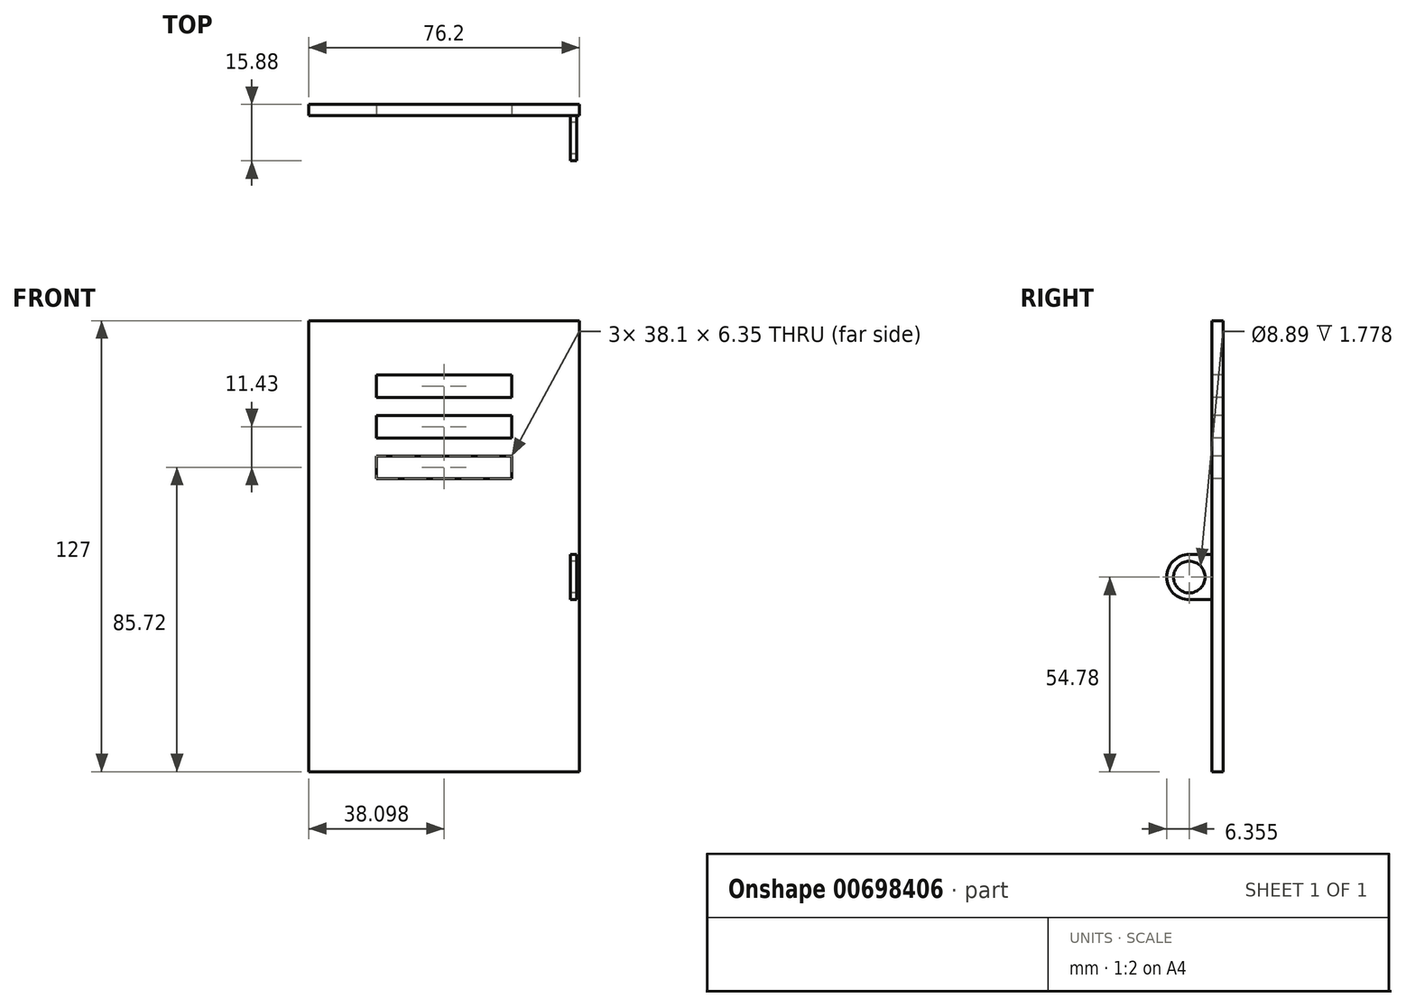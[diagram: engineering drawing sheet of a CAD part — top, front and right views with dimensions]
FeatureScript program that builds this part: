
annotation { "Feature Type Name" : "Feature", "Feature Type Description" : "" }
export const myFeature = defineFeature(function(context is Context, id is Id, definition is map)
    precondition{}
    {
        {
            var Q0;
            Q0=qCreatedBy(makeId("Front.planeOp"),FACE);
            var sketch = newSketch(context, id + "F0", { "sketchPlane" : qUnion([Q0])});
            skLineSegment(sketch, "E0.bottom", {"start": v(-36.9, 78.57) * mm, "end": v(39.3, 78.57) * mm});
            skLineSegment(sketch, "E0.top", {"start": v(-36.9, -48.43) * mm, "end": v(39.3, -48.43) * mm});
            skLineSegment(sketch, "E0.left", {"start": v(-36.9, 78.57) * mm, "end": v(-36.9, -48.43) * mm});
            skLineSegment(sketch, "E0.right", {"start": v(39.3, 78.57) * mm, "end": v(39.3, -48.43) * mm});
            skSolve(sketch);
        }
        {
            var Q0;
            Q0=makeQuery(id+"F0.imprint","IMPRINT",FACE,{"disambiguationData":[TD([[makeQuery(id+"F0.imprint","IMPRINT",EDGE,{"derivedFrom":sQuery(id+"F0.wireOp",EDGE,"E0.bottom")}),-1.0]])]});
            extrude(context, id + "F1", {"entities" : qUnion([Q0]), "depth" : 3.17 * mm, "offsetDistance" : 25.4 * mm});
        }
        {
            var Q0;
            Q0=makeQuery(id+"F1.opExtrude","CAP_FACE",FACE,{"disambiguationData":[OSD([sQuery(id+"F0.wireOp",EDGE,"E0.bottom"),sQuery(id+"F0.wireOp",EDGE,"E0.top"),sQuery(id+"F0.wireOp",EDGE,"E0.left"),sQuery(id+"F0.wireOp",EDGE,"E0.right")])],"isStart":false});
            var sketch = newSketch(context, id + "F2", { "sketchPlane" : qUnion([Q0])});
            skLineSegment(sketch, "E1.bottom", {"start": v(-17.84, 63.33) * mm, "end": v(20.26, 63.33) * mm});
            skLineSegment(sketch, "E1.top", {"start": v(-17.84, 56.98) * mm, "end": v(20.26, 56.98) * mm});
            skLineSegment(sketch, "E1.left", {"start": v(-17.84, 63.33) * mm, "end": v(-17.84, 56.98) * mm});
            skLineSegment(sketch, "E1.right", {"start": v(20.26, 63.33) * mm, "end": v(20.26, 56.98) * mm});
            skLineSegment(sketch, "E2.bottom", {"start": v(-17.84, 51.9) * mm, "end": v(20.26, 51.9) * mm});
            skLineSegment(sketch, "E2.top", {"start": v(-17.84, 45.55) * mm, "end": v(20.26, 45.55) * mm});
            skLineSegment(sketch, "E2.left", {"start": v(-17.84, 51.9) * mm, "end": v(-17.84, 45.55) * mm});
            skLineSegment(sketch, "E2.right", {"start": v(20.26, 51.9) * mm, "end": v(20.26, 45.55) * mm});
            skLineSegment(sketch, "E3.bottom", {"start": v(-17.84, 40.47) * mm, "end": v(20.26, 40.47) * mm});
            skLineSegment(sketch, "E3.top", {"start": v(-17.84, 34.12) * mm, "end": v(20.26, 34.12) * mm});
            skLineSegment(sketch, "E3.left", {"start": v(-17.84, 40.47) * mm, "end": v(-17.84, 34.12) * mm});
            skLineSegment(sketch, "E3.right", {"start": v(20.26, 40.47) * mm, "end": v(20.26, 34.12) * mm});
            skSolve(sketch);
        }
        {
            var Q0;
            Q0=makeQuery(id+"F2.imprint","IMPRINT",FACE,{"disambiguationData":[TD([[makeQuery(id+"F2.imprint","IMPRINT",EDGE,{"derivedFrom":sQuery(id+"F2.wireOp",EDGE,"E1.bottom")}),-1.0]])]});
            var Q1;
            Q1=makeQuery(id+"F2.imprint","IMPRINT",FACE,{"disambiguationData":[TD([[makeQuery(id+"F2.imprint","IMPRINT",EDGE,{"derivedFrom":sQuery(id+"F2.wireOp",EDGE,"E2.bottom")}),-1.0]])]});
            var Q2;
            Q2=makeQuery(id+"F2.imprint","IMPRINT",FACE,{"disambiguationData":[TD([[makeQuery(id+"F2.imprint","IMPRINT",EDGE,{"derivedFrom":sQuery(id+"F2.wireOp",EDGE,"E3.bottom")}),-1.0]])]});
            extrude(context, id + "F3", {"entities" : qUnion([Q0, Q1, Q2]), "operationType" : NewBodyOperationType.REMOVE, "oppositeDirection" : true, "depth" : 3.17 * mm, "offsetDistance" : 25.4 * mm});
        }
        {
            var Q0;
            Q0=makeQuery(id+"F1.opExtrude","CAP_FACE",FACE,{"disambiguationData":[OSD([sQuery(id+"F0.wireOp",EDGE,"E0.bottom"),sQuery(id+"F0.wireOp",EDGE,"E0.top"),sQuery(id+"F0.wireOp",EDGE,"E0.left"),sQuery(id+"F0.wireOp",EDGE,"E0.right")])],"isStart":false});
            var sketch = newSketch(context, id + "F4", { "sketchPlane" : qUnion([Q0])});
            skLineSegment(sketch, "E4.bottom", {"start": v(38.55, 12.7) * mm, "end": v(36.77, 12.7) * mm});
            skLineSegment(sketch, "E4.top", {"start": v(38.55, 0) * mm, "end": v(36.77, 0) * mm});
            skLineSegment(sketch, "E4.left", {"start": v(38.55, 12.7) * mm, "end": v(38.55, 0) * mm});
            skLineSegment(sketch, "E4.right", {"start": v(36.77, 12.7) * mm, "end": v(36.77, 0) * mm});
            skSolve(sketch);
        }
        {
            var Q0;
            Q0=makeQuery(id+"F4.imprint","IMPRINT",FACE,{"disambiguationData":[TD([[makeQuery(id+"F4.imprint","IMPRINT",EDGE,{"derivedFrom":sQuery(id+"F4.wireOp",EDGE,"E4.bottom")}),1.0]])]});
            extrude(context, id + "F5", {"entities" : qUnion([Q0]), "operationType" : NewBodyOperationType.ADD, "depth" : 12.7 * mm, "offsetDistance" : 25.4 * mm});
        }
        {
            var Q0;
            Q0=makeQuery(id+"F5.opExtrude","CAP_EDGE",EDGE,{"disambiguationData":[OSD([sQuery(id+"F4.wireOp",EDGE,"E4.bottom")])],"isStart":false});
            fillet(context, id + "F6", {"entities" : qUnion([Q0]), "radius" : 6.35 * mm, "tangentPropagation" : true, "allowEdgeOverflow" : false});
        }
        {
            var Q0;
            Q0=makeQuery(id+"F5.opExtrude","CAP_EDGE",EDGE,{"disambiguationData":[OSD([sQuery(id+"F4.wireOp",EDGE,"E4.top")])],"isStart":false});
            fillet(context, id + "F7", {"entities" : qUnion([Q0]), "radius" : 6.35 * mm, "tangentPropagation" : true, "allowEdgeOverflow" : false});
        }
        {
            var Q0;
            Q0=makeQuery(id+"F5.opExtrude","SWEPT_FACE",FACE,{"disambiguationData":[OSD([sQuery(id+"F4.wireOp",EDGE,"E4.right")])]});
            var sketch = newSketch(context, id + "F8", { "sketchPlane" : qUnion([Q0])});
            skCircle(sketch, "E5", {"center": v(9.52, 6.35) * mm, "radius": 4.45 * mm});
            skSolve(sketch);
        }
        {
            var Q0;
            Q0=makeQuery(id+"F8.imprint","IMPRINT",FACE,{"disambiguationData":[TD([[makeQuery(id+"F8.imprint","IMPRINT",EDGE,{"derivedFrom":sQuery(id+"F8.wireOp",EDGE,"E5")}),1.0]])]});
            extrude(context, id + "F9", {"entities" : qUnion([Q0]), "operationType" : NewBodyOperationType.REMOVE, "oppositeDirection" : true, "depth" : 25.4 * mm, "offsetDistance" : 25.4 * mm});
        }
    });
